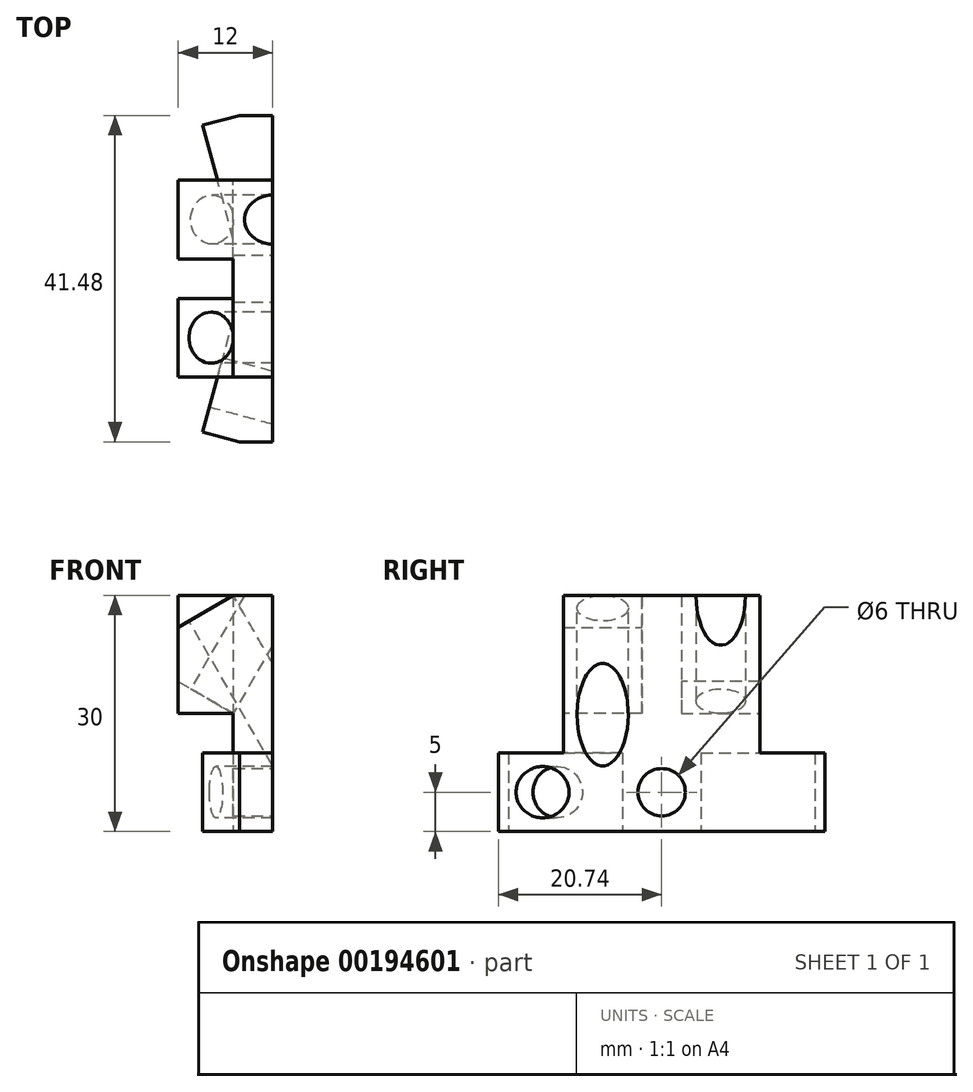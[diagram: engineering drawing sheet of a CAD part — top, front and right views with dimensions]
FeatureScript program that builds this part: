
annotation { "Feature Type Name" : "Feature", "Feature Type Description" : "" }
export const myFeature = defineFeature(function(context is Context, id is Id, definition is map)
    precondition{}
    {
        {
            var Q0;
            Q0=qCreatedBy(makeId("Front.planeOp"),FACE);
            var sketch = newSketch(context, id + "F0", { "sketchPlane" : qUnion([Q0])});
            skLineSegment(sketch, "E0.bottom", {"start": v(-5, 2.5) * mm, "end": v(5, 2.5) * mm});
            skLineSegment(sketch, "E0.top", {"start": v(-5, -2.5) * mm, "end": v(5, -2.5) * mm});
            skLineSegment(sketch, "E0.left", {"start": v(-5, 2.5) * mm, "end": v(-5, -2.5) * mm});
            skLineSegment(sketch, "E0.right", {"start": v(5, 2.5) * mm, "end": v(5, -2.5) * mm});
            skPoint(sketch, "E0.middle", {"position": v(0, 0) * mm});
            skSolve(sketch);
        }
        {
            var Q0;
            Q0 = qSketchRegion(id + "F0", true);
            extrude(context, id + "F1", {"entities" : qUnion([Q0]), "depth" : 5 * mm, "hasSecondDirection" : true, "secondDirectionOppositeDirection" : true, "secondDirectionDepth" : 5 * mm});
        }
        {
            var Q0;
            Q0=makeQuery(id+"F1.opExtrude","SWEPT_FACE",FACE,{"disambiguationData":[OSD([sQuery(id+"F0.wireOp",EDGE,"E0.bottom")])]});
            var sketch = newSketch(context, id + "F2", { "sketchPlane" : qUnion([Q0])});
            skCircle(sketch, "E1", {"center": v(0, 0) * mm, "radius": 1.75 * mm});
            skSolve(sketch);
        }
        {
            var Q0;
            Q0 = qSketchRegion(id + "F2", true);
            extrude(context, id + "F3", {"entities" : qUnion([Q0]), "operationType" : NewBodyOperationType.REMOVE, "endBound" : BoundingType.UP_TO_NEXT, "oppositeDirection" : true, "depth" : 25 * mm});
        }
        {
            var Q0;
            Q0=makeQuery(id+"F1.opExtrude","CAP_FACE",FACE,{"disambiguationData":[OSD([sQuery(id+"F0.wireOp",EDGE,"E0.bottom"),sQuery(id+"F0.wireOp",EDGE,"E0.top"),sQuery(id+"F0.wireOp",EDGE,"E0.left"),sQuery(id+"F0.wireOp",EDGE,"E0.right")])],"isStart":false});
            var sketch = newSketch(context, id + "F4", { "sketchPlane" : qUnion([Q0])});
            skLineSegment(sketch, "E2", {"start": v(-5, 2.5) * mm, "end": v(-10, 2.5) * mm, "construction": true});
            skLineSegment(sketch, "E3", {"start": v(-10, 2.5) * mm, "end": v(-5, -2.5) * mm});
            skLineSegment(sketch, "E4", {"start": v(-5, -2.5) * mm, "end": v(-5, 2.5) * mm});
            skLineSegment(sketch, "E5.bottom", {"start": v(-5, 2.5) * mm, "end": v(-10, 2.5) * mm});
            skLineSegment(sketch, "E5.top", {"start": v(-5, 57.5) * mm, "end": v(-10, 57.5) * mm});
            skLineSegment(sketch, "E5.left", {"start": v(-5, 2.5) * mm, "end": v(-5, 57.5) * mm});
            skLineSegment(sketch, "E5.right", {"start": v(-10, 2.5) * mm, "end": v(-10, 57.5) * mm});
            skLineSegment(sketch, "E6.bottom", {"start": v(-5, 29.5) * mm, "end": v(21, 29.5) * mm});
            skLineSegment(sketch, "E6.top", {"start": v(-5, 55.5) * mm, "end": v(21, 55.5) * mm});
            skLineSegment(sketch, "E6.left", {"start": v(-5, 29.5) * mm, "end": v(-5, 55.5) * mm});
            skLineSegment(sketch, "E6.right", {"start": v(21, 29.5) * mm, "end": v(21, 55.5) * mm});
            skLineSegment(sketch, "E7.bottom", {"start": v(-5, 57.5) * mm, "end": v(23, 57.5) * mm});
            skLineSegment(sketch, "E7.top", {"start": v(-5, 27.5) * mm, "end": v(23, 27.5) * mm});
            skLineSegment(sketch, "E7.left", {"start": v(-5, 57.5) * mm, "end": v(-5, 27.5) * mm});
            skLineSegment(sketch, "E7.right", {"start": v(23, 57.5) * mm, "end": v(23, 27.5) * mm});
            skSolve(sketch);
        }
        {
            var Q0;
            Q0=makeQuery(id+"F4.imprint","IMPRINT",FACE,{"disambiguationData":[TD([[makeQuery(id+"F4.imprint","IMPRINT",EDGE,{"derivedFrom":sQuery(id+"F4.wireOp",EDGE,"E3")}),1.0]])]});
            var Q1;
            Q1=makeQuery(id+"F4.imprint","IMPRINT",FACE,{"disambiguationData":[TD([[makeQuery(id+"F4.imprint","IMPRINT",EDGE,{"derivedFrom":sQuery(id+"F4.wireOp",EDGE,"E5.bottom")}),-1.0]])]});
            var Q2;
            {var subQ2=sQuery(id+"F4.wireOp",EDGE,"E6.bottom");Q2=makeQuery(id+"F4.imprint","IMPRINT",FACE,{"disambiguationData":[TD([[makeQuery(id+"F4.imprint","IMPRINT",EDGE,{"derivedFrom":subQ2}),-1.0]])]});}
            var Q3;
            Q3=makeQuery(id+"F1.opExtrude","CAP_FACE",FACE,{"disambiguationData":[OSD([sQuery(id+"F0.wireOp",EDGE,"E0.bottom"),sQuery(id+"F0.wireOp",EDGE,"E0.top"),sQuery(id+"F0.wireOp",EDGE,"E0.left"),sQuery(id+"F0.wireOp",EDGE,"E0.right")])],"isStart":true});
            extrude(context, id + "F5", {"entities" : qUnion([Q0, Q1, Q2]), "operationType" : NewBodyOperationType.ADD, "endBound" : BoundingType.UP_TO_SURFACE, "oppositeDirection" : true, "endBoundEntityFace" : qUnion([Q3]), "depth" : 25 * mm});
        }
        {
            var Q0;
            Q0=makeQuery(id+"F5.opExtrude","SWEPT_FACE",FACE,{"disambiguationData":[OSD([sQuery(id+"F4.wireOp",EDGE,"E5.top"),sQuery(id+"F4.wireOp",EDGE,"E7.bottom")])]});
            var sketch = newSketch(context, id + "F6", { "sketchPlane" : qUnion([Q0])});
            skLineSegment(sketch, "E8.bottom", {"start": v(23, 5) * mm, "end": v(18, 5) * mm});
            skLineSegment(sketch, "E8.top", {"start": v(23, -5) * mm, "end": v(18, -5) * mm});
            skLineSegment(sketch, "E8.left", {"start": v(23, 5) * mm, "end": v(23, -5) * mm});
            skLineSegment(sketch, "E8.right", {"start": v(18, 5) * mm, "end": v(18, -5) * mm});
            skLineSegment(sketch, "E9", {"start": v(18, 5) * mm, "end": v(14.12, 19.49) * mm});
            skLineSegment(sketch, "E10", {"start": v(14.12, 19.49) * mm, "end": v(18.78, 20.74) * mm});
            skLineSegment(sketch, "E11", {"start": v(18.78, 20.74) * mm, "end": v(23, 5) * mm});
            skLineSegment(sketch, "E12.MirrorCS", {"start": v(14.12, -19.49) * mm, "end": v(18.78, -20.74) * mm});
            skLineSegment(sketch, "E13.MirrorCS", {"start": v(18, -5) * mm, "end": v(14.12, -19.49) * mm});
            skLineSegment(sketch, "E14.MirrorCS", {"start": v(18.78, -20.74) * mm, "end": v(23, -5) * mm});
            skPoint(sketch, "E15.MirrorCS.start.orphan", {"position": v(18.78, 20.74) * mm});
            skPoint(sketch, "E16.MirrorCS.end.orphan", {"position": v(23, 5) * mm});
            skLineSegment(sketch, "E17", {"start": v(23, 5) * mm, "end": v(23, 20.74) * mm});
            skLineSegment(sketch, "E18", {"start": v(23, 20.74) * mm, "end": v(18.78, 20.74) * mm});
            skLineSegment(sketch, "E19", {"start": v(23, -5) * mm, "end": v(23, -20.74) * mm});
            skLineSegment(sketch, "E20", {"start": v(23, -20.74) * mm, "end": v(18.78, -20.74) * mm});
            skSolve(sketch);
        }
        {
            var Q0;
            Q0=makeQuery(id+"F6.imprint","IMPRINT",FACE,{"disambiguationData":[TD([[makeQuery(id+"F6.imprint","IMPRINT",EDGE,{"derivedFrom":sQuery(id+"F6.wireOp",EDGE,"E8.bottom")}),-1.0]])]});
            var Q1;
            Q1=makeQuery(id+"F6.imprint","IMPRINT",FACE,{"disambiguationData":[TD([[makeQuery(id+"F6.imprint","IMPRINT",EDGE,{"derivedFrom":sQuery(id+"F6.wireOp",EDGE,"E8.top")}),1.0]])]});
            var Q2;
            Q2=makeQuery(id+"F6.imprint","IMPRINT",FACE,{"disambiguationData":[TD([[makeQuery(id+"F6.imprint","IMPRINT",EDGE,{"derivedFrom":sQuery(id+"F6.wireOp",EDGE,"E12.MirrorCS")}),-1.0]])]});
            var Q3;
            Q3=makeQuery(id+"F6.imprint","IMPRINT",FACE,{"disambiguationData":[TD([[makeQuery(id+"F6.imprint","IMPRINT",EDGE,{"derivedFrom":sQuery(id+"F6.wireOp",EDGE,"E8.bottom")}),1.0]])]});
            var Q4;
            Q4=makeQuery(id+"F6.imprint","IMPRINT",FACE,{"disambiguationData":[TD([[makeQuery(id+"F6.imprint","IMPRINT",EDGE,{"derivedFrom":sQuery(id+"F6.wireOp",EDGE,"E10")}),1.0]])]});
            var Q5;
            Q5=makeQuery(id+"F6.imprint","IMPRINT",FACE,{"disambiguationData":[TD([[makeQuery(id+"F6.imprint","IMPRINT",EDGE,{"derivedFrom":sQuery(id+"F6.wireOp",EDGE,"E14.MirrorCS")}),-1.0]])]});
            var Q6;
            Q6=makeQuery(id+"F6.imprint","IMPRINT",FACE,{"disambiguationData":[TD([[makeQuery(id+"F6.imprint","IMPRINT",EDGE,{"derivedFrom":sQuery(id+"F6.wireOp",EDGE,"E11")}),1.0]])]});
            extrude(context, id + "F7", {"entities" : qUnion([Q0, Q1, Q2, Q3, Q4, Q5, Q6]), "operationType" : NewBodyOperationType.ADD, "depth" : 10 * mm});
        }
        {
            var Q0;
            Q0=makeQuery(id+"F7.boolean.opBoolean","MERGE",FACE,{"derivedFrom":[makeQuery(id+"F5.opExtrude","SWEPT_FACE",FACE,{"disambiguationData":[OSD([sQuery(id+"F4.wireOp",EDGE,"E7.right")])]}),makeQuery(id+"F7.opExtrude","SWEPT_FACE",FACE,{"disambiguationData":[OSD([sQuery(id+"F6.wireOp",EDGE,"E8.left"),sQuery(id+"F6.wireOp",EDGE,"Zx6JNSOK-Eq2F-A8kR-0zWC-YJmkVr3cmCwT"),sQuery(id+"F6.wireOp",EDGE,"98d5ecce-5735-4c8a-99ee-9f374a27924c0.MirrorCS")])]})]});
            var sketch = newSketch(context, id + "F8", { "sketchPlane" : qUnion([Q0])});
            skCircle(sketch, "E21", {"center": v(0, 62.5) * mm, "radius": 3 * mm});
            skSolve(sketch);
        }
        {
            var Q0;
            Q0 = qSketchRegion(id + "F8", true);
            extrude(context, id + "F9", {"entities" : qUnion([Q0]), "operationType" : NewBodyOperationType.REMOVE, "endBound" : BoundingType.UP_TO_NEXT, "oppositeDirection" : true, "depth" : 25 * mm});
        }
        {
            var Q0;
            Q0=makeQuery(id+"F7.opExtrude","SWEPT_FACE",FACE,{"disambiguationData":[OSD([sQuery(id+"F6.wireOp",EDGE,"E13.MirrorCS")])]});
            var sketch = newSketch(context, id + "F10", { "sketchPlane" : qUnion([Q0])});
            skCircle(sketch, "E22", {"center": v(8.67, 62.5) * mm, "radius": 3.25 * mm});
            skSolve(sketch);
        }
        {
            var Q0;
            Q0=makeQuery(id+"F10.imprint","IMPRINT",FACE,{"disambiguationData":[TD([[makeQuery(id+"F10.imprint","IMPRINT",EDGE,{"derivedFrom":sQuery(id+"F10.wireOp",EDGE,"E22")}),1.0]])]});
            extrude(context, id + "F11", {"entities" : qUnion([Q0]), "operationType" : NewBodyOperationType.REMOVE, "endBound" : BoundingType.UP_TO_NEXT, "oppositeDirection" : true, "depth" : 25 * mm});
        }
        {
            var Q0;
            Q0=makeQuery(id+"F7.opExtrude","CAP_FACE",FACE,{"disambiguationData":[OSD([sQuery(id+"F6.wireOp",EDGE,"E8.left"),sQuery(id+"F6.wireOp",EDGE,"E8.right"),sQuery(id+"F6.wireOp",EDGE,"E9"),sQuery(id+"F6.wireOp",EDGE,"E10"),sQuery(id+"F6.wireOp",EDGE,"E12.MirrorCS"),sQuery(id+"F6.wireOp",EDGE,"E13.MirrorCS"),sQuery(id+"F6.wireOp",EDGE,"E17"),sQuery(id+"F6.wireOp",EDGE,"E18"),sQuery(id+"F6.wireOp",EDGE,"E19"),sQuery(id+"F6.wireOp",EDGE,"E20")])],"isStart":false});
            var sketch = newSketch(context, id + "F12", { "sketchPlane" : qUnion([Q0])});
            skLineSegment(sketch, "E23", {"start": v(23, 0) * mm, "end": v(18, 0) * mm, "construction": true});
            skLineSegment(sketch, "E24.bottom", {"start": v(23, -12.5) * mm, "end": v(18, -12.5) * mm});
            skLineSegment(sketch, "E24.top", {"start": v(23, 12.5) * mm, "end": v(18, 12.5) * mm});
            skLineSegment(sketch, "E24.left", {"start": v(23, -12.5) * mm, "end": v(23, 12.5) * mm});
            skLineSegment(sketch, "E24.right", {"start": v(18, -12.5) * mm, "end": v(18, 12.5) * mm});
            skPoint(sketch, "E24.middle", {"position": v(20.5, 0) * mm});
            skSolve(sketch);
        }
        {
            var Q0;
            Q0 = qSketchRegion(id + "F12", true);
            extrude(context, id + "F13", {"entities" : qUnion([Q0]), "operationType" : NewBodyOperationType.ADD, "depth" : 20 * mm});
        }
        {
            var Q0;
            Q0=makeQuery(id+"F13.opExtrude","SWEPT_FACE",FACE,{"disambiguationData":[OSD([sQuery(id+"F12.wireOp",EDGE,"E24.top")])]});
            var sketch = newSketch(context, id + "F14", { "sketchPlane" : qUnion([Q0])});
            skLineSegment(sketch, "E25", {"start": v(-18, 72.5) * mm, "end": v(-18, 82.5) * mm});
            skLineSegment(sketch, "E26", {"start": v(-18, 82.5) * mm, "end": v(-0.68, 82.5) * mm});
            skLineSegment(sketch, "E27", {"start": v(-0.68, 82.5) * mm, "end": v(-18, 72.5) * mm});
            skSolve(sketch);
        }
        {
            var Q0;
            Q0=makeQuery(id+"F14.imprint","IMPRINT",FACE,{"disambiguationData":[TD([[makeQuery(id+"F14.imprint","IMPRINT",EDGE,{"derivedFrom":sQuery(id+"F14.wireOp",EDGE,"E25")}),1.0]])]});
            extrude(context, id + "F15", {"entities" : qUnion([Q0]), "operationType" : NewBodyOperationType.ADD, "oppositeDirection" : true, "depth" : 10 * mm});
        }
        {
            var Q0;
            Q0=makeQuery(id+"F13.opExtrude","SWEPT_FACE",FACE,{"disambiguationData":[OSD([sQuery(id+"F12.wireOp",EDGE,"E24.bottom")])]});
            var sketch = newSketch(context, id + "F16", { "sketchPlane" : qUnion([Q0])});
            skLineSegment(sketch, "E28", {"start": v(18, 87.5) * mm, "end": v(18, 77.5) * mm});
            skLineSegment(sketch, "E29", {"start": v(18, 77.5) * mm, "end": v(0.68, 77.5) * mm});
            skLineSegment(sketch, "E30", {"start": v(0.68, 77.5) * mm, "end": v(18, 87.5) * mm});
            skSolve(sketch);
        }
        {
            var Q0;
            Q0 = qSketchRegion(id + "F16", true);
            extrude(context, id + "F17", {"entities" : qUnion([Q0]), "operationType" : NewBodyOperationType.ADD, "oppositeDirection" : true, "depth" : 10 * mm});
        }
        {
            var Q0;
            Q0=makeQuery(id+"F17.opExtrude","SWEPT_FACE",FACE,{"disambiguationData":[OSD([sQuery(id+"F16.wireOp",EDGE,"E29")])]});
            var sketch = newSketch(context, id + "F18", { "sketchPlane" : qUnion([Q0])});
            skLineSegment(sketch, "E31.bottom", {"start": v(18, 12.5) * mm, "end": v(11, 12.5) * mm});
            skLineSegment(sketch, "E31.top", {"start": v(18, 2.5) * mm, "end": v(11, 2.5) * mm});
            skLineSegment(sketch, "E31.left", {"start": v(18, 12.5) * mm, "end": v(18, 2.5) * mm});
            skLineSegment(sketch, "E31.right", {"start": v(11, 12.5) * mm, "end": v(11, 2.5) * mm});
            skSolve(sketch);
        }
        {
            var Q0;
            Q0 = qSketchRegion(id + "F18", true);
            extrude(context, id + "F19", {"entities" : qUnion([Q0]), "operationType" : NewBodyOperationType.ADD, "depth" : 5 * mm});
        }
        {
            var Q0;
            Q0=makeQuery(id+"F17.opExtrude","SWEPT_FACE",FACE,{"disambiguationData":[OSD([sQuery(id+"F16.wireOp",EDGE,"E29")])]});
            extrude(context, id + "F20", {"entities" : qUnion([Q0]), "operationType" : NewBodyOperationType.REMOVE, "oppositeDirection" : true, "depth" : 25 * mm});
        }
        {
            var Q0;
            Q0=makeQuery(id+"F17.opExtrude","SWEPT_FACE",FACE,{"disambiguationData":[OSD([sQuery(id+"F16.wireOp",EDGE,"E30")])]});
            var sketch = newSketch(context, id + "F21", { "sketchPlane" : qUnion([Q0])});
            skLineSegment(sketch, "E32", {"start": v(56.09, -2.5) * mm, "end": v(56.09, -12.5) * mm, "construction": true});
            skCircle(sketch, "E33", {"center": v(56.09, -7.5) * mm, "radius": 3.25 * mm});
            skSolve(sketch);
        }
        {
            var Q0;
            Q0 = qSketchRegion(id + "F21", true);
            extrude(context, id + "F22", {"entities" : qUnion([Q0]), "operationType" : NewBodyOperationType.REMOVE, "endBound" : BoundingType.UP_TO_NEXT, "oppositeDirection" : true, "depth" : 25 * mm});
        }
        {
            var Q0;
            Q0=makeQuery(id+"F15.opExtrude","SWEPT_FACE",FACE,{"disambiguationData":[OSD([sQuery(id+"F14.wireOp",EDGE,"E26")])]});
            var sketch = newSketch(context, id + "F23", { "sketchPlane" : qUnion([Q0])});
            skLineSegment(sketch, "E34.bottom", {"start": v(18, 2.5) * mm, "end": v(11, 2.5) * mm});
            skLineSegment(sketch, "E34.top", {"start": v(18, 12.5) * mm, "end": v(11, 12.5) * mm});
            skLineSegment(sketch, "E34.left", {"start": v(18, 2.5) * mm, "end": v(18, 12.5) * mm});
            skLineSegment(sketch, "E34.right", {"start": v(11, 2.5) * mm, "end": v(11, 12.5) * mm});
            skSolve(sketch);
        }
        {
            var Q0;
            Q0 = qSketchRegion(id + "F23", true);
            extrude(context, id + "F24", {"entities" : qUnion([Q0]), "operationType" : NewBodyOperationType.ADD, "depth" : 5 * mm});
        }
        {
            var Q0;
            Q0=makeQuery(id+"F15.opExtrude","SWEPT_FACE",FACE,{"disambiguationData":[OSD([sQuery(id+"F14.wireOp",EDGE,"E27")])]});
            var sketch = newSketch(context, id + "F25", { "sketchPlane" : qUnion([Q0])});
            skLineSegment(sketch, "E35", {"start": v(-23.79, -12.5) * mm, "end": v(-23.79, -2.5) * mm, "construction": true});
            skCircle(sketch, "E36", {"center": v(-23.79, -7.5) * mm, "radius": 3.12 * mm});
            skSolve(sketch);
        }
        {
            var Q0;
            Q0=makeQuery(id+"F25.imprint","IMPRINT",FACE,{"disambiguationData":[TD([[makeQuery(id+"F25.imprint","IMPRINT",EDGE,{"derivedFrom":sQuery(id+"F25.wireOp",EDGE,"E36")}),1.0]])]});
            extrude(context, id + "F26", {"entities" : qUnion([Q0]), "operationType" : NewBodyOperationType.REMOVE, "endBound" : BoundingType.UP_TO_NEXT, "oppositeDirection" : true, "depth" : 25 * mm});
        }
        {
            var Q0;
            Q0=makeQuery(id+"F15.opExtrude","SWEPT_FACE",FACE,{"disambiguationData":[OSD([sQuery(id+"F14.wireOp",EDGE,"E26")])]});
            extrude(context, id + "F27", {"entities" : qUnion([Q0]), "operationType" : NewBodyOperationType.REMOVE, "endBound" : BoundingType.UP_TO_NEXT, "oppositeDirection" : true, "depth" : 25 * mm});
        }
        {
            var Q0;
            Q0=makeQuery(id+"F5.opExtrude","SWEPT_FACE",FACE,{"disambiguationData":[OSD([sQuery(id+"F4.wireOp",EDGE,"E5.top"),sQuery(id+"F4.wireOp",EDGE,"E7.bottom")])]});
            extrude(context, id + "F28", {"entities" : qUnion([Q0]), "operationType" : NewBodyOperationType.REMOVE, "endBound" : BoundingType.THROUGH_ALL, "oppositeDirection" : true, "depth" : 25 * mm});
        }
        {
            var Q0;
            Q0=makeQuery(id+"F5.opExtrude","SWEPT_FACE",FACE,{"disambiguationData":[OSD([sQuery(id+"F4.wireOp",EDGE,"E7.top")])]});
            var Q1;
            {var subQ3=sQuery(id+"F6.wireOp",EDGE,"E19");var subQ4=sQuery(id+"F6.wireOp",EDGE,"E17");var subQ5=sQuery(id+"F6.wireOp",EDGE,"E8.left");var subQ6=sQuery(id+"F6.wireOp",EDGE,"E12.MirrorCS");var subQ7=sQuery(id+"F6.wireOp",EDGE,"E8.right");var subQ8=sQuery(id+"F6.wireOp",EDGE,"E13.MirrorCS");var subQ9=sQuery(id+"F6.wireOp",EDGE,"E20");Q1=makeQuery(id+"F7.boolean.opBoolean","SPLIT",FACE,{"disambiguationData":[TD([makeQuery(id+"F7.opExtrude","SWEPT_FACE",FACE,{"disambiguationData":[OSD([subQ6])]})])],"derivedFrom":makeQuery(id+"F7.opExtrude","CAP_FACE",FACE,{"disambiguationData":[OSD([subQ5,subQ7,sQuery(id+"F6.wireOp",EDGE,"E9"),sQuery(id+"F6.wireOp",EDGE,"E10"),subQ6,subQ8,subQ4,sQuery(id+"F6.wireOp",EDGE,"E18"),subQ3,subQ9])],"isStart":true})});}
            extrude(context, id + "F29", {"entities" : qUnion([Q0]), "operationType" : NewBodyOperationType.REMOVE, "endBound" : BoundingType.UP_TO_SURFACE, "oppositeDirection" : true, "endBoundEntityFace" : qUnion([Q1]), "depth" : 25 * mm});
        }
    });
